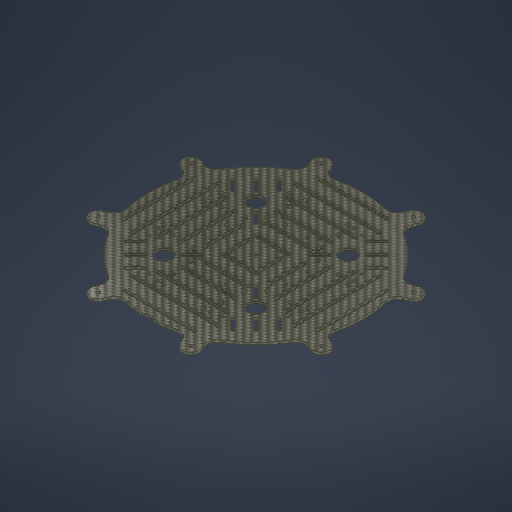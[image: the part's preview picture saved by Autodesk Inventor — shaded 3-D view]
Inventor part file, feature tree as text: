
AUTODESK INVENTOR PART (.ipt)
format: ipt  version: 2025 (Build 290162010, 162A)  size: 922,112 bytes
history: native  units: mm
features: extrude x1, sketch x1
ambient origin geometry x8: Origin, YZ Plane, XZ Plane, XY Plane, X Axis, Y Axis, Z Axis, Center Point
bodies: Solid1 (feature_tree)
feature tree (2):
  extrude  "Extrusion1"  [1 undecoded]
  sketch  "Sketch1"  dims[d0=2.0mm d1=0.0mm]
note: 1 required parameter value undecoded (feature->parameter linkage not recoverable at this tier; creation-order binding heuristic only, values carry confidence <= 0.55)
